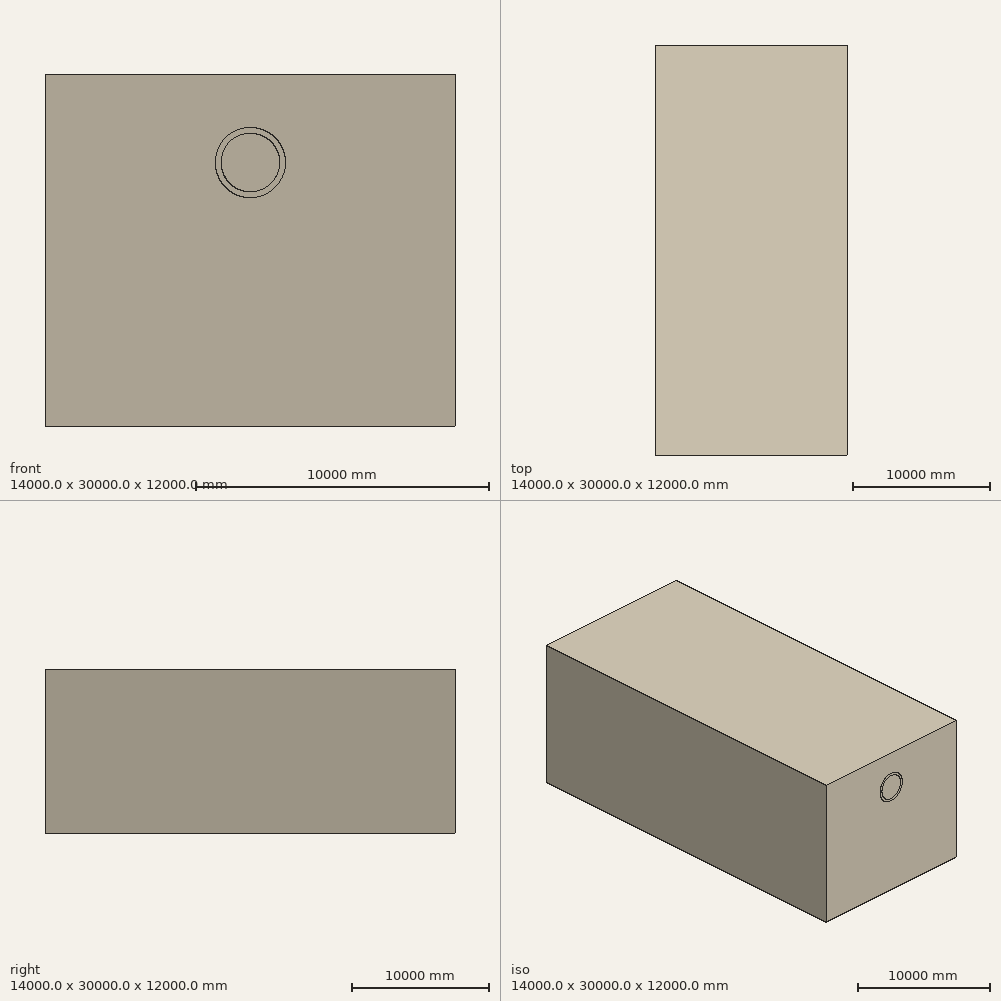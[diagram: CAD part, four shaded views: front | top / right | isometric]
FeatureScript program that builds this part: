
annotation { "Feature Type Name" : "Feature", "Feature Type Description" : "" }
export const myFeature = defineFeature(function(context is Context, id is Id, definition is map)
    precondition{}
    {
        {
            var Q0;
            Q0=qCreatedBy(makeId("Front.planeOp"),FACE);
            var sketch = newSketch(context, id + "F0", { "sketchPlane" : qUnion([Q0])});
            skCircle(sketch, "E0", {"center": v(0, 0) * mm, "radius": 1000 * mm});
            skLineSegment(sketch, "E1.bottom", {"start": v(-7000, 3000) * mm, "end": v(7000, 3000) * mm});
            skLineSegment(sketch, "E1.top", {"start": v(-7000, -9000) * mm, "end": v(7000, -9000) * mm});
            skLineSegment(sketch, "E1.left", {"start": v(-7000, 3000) * mm, "end": v(-7000, -9000) * mm});
            skLineSegment(sketch, "E1.right", {"start": v(7000, 3000) * mm, "end": v(7000, -9000) * mm});
            skCircle(sketch, "E2", {"center": v(0, 0) * mm, "radius": 1200 * mm});
            skSolve(sketch);
        }
        {
            var Q0;
            Q0=makeQuery(id+"F0.imprint","IMPRINT",FACE,{"disambiguationData":[TD([[makeQuery(id+"F0.imprint","IMPRINT",EDGE,{"derivedFrom":sQuery(id+"F0.wireOp",EDGE,"E1.bottom")}),-1.0]])]});
            extrude(context, id + "F1", {"entities" : qUnion([Q0]), "depth" : 30000 * mm, "offsetDistance" : 25 * mm});
        }
        {
            var Q0;
            Q0=makeQuery(id+"F1.opExtrude","CAP_FACE",FACE,{"disambiguationData":[OSD([sQuery(id+"F0.wireOp",EDGE,"E1.bottom"),sQuery(id+"F0.wireOp",EDGE,"E1.top"),sQuery(id+"F0.wireOp",EDGE,"E1.left"),sQuery(id+"F0.wireOp",EDGE,"E1.right"),sQuery(id+"F0.wireOp",EDGE,"E2")])],"isStart":true});
            var sketch = newSketch(context, id + "F2", { "sketchPlane" : qUnion([Q0])});
            skCircle(sketch, "E3", {"center": v(0, 0) * mm, "radius": 1200 * mm});
            skCircle(sketch, "E4", {"center": v(0, 0) * mm, "radius": 1000 * mm});
            skSolve(sketch);
        }
        {
            var Q0;
            Q0=makeQuery(id+"F2.imprint","IMPRINT",FACE,{"disambiguationData":[TD([[makeQuery(id+"F2.imprint","IMPRINT",EDGE,{"derivedFrom":sQuery(id+"F2.wireOp",EDGE,"E3")}),-1.0]])]});
            extrude(context, id + "F3", {"entities" : qUnion([Q0]), "depth" : -30000 * mm, "offsetDistance" : 25 * mm});
        }
        {
            var Q0;
            Q0=makeQuery(id+"F1.opExtrude","CAP_FACE",FACE,{"disambiguationData":[OSD([sQuery(id+"F0.wireOp",EDGE,"E1.bottom"),sQuery(id+"F0.wireOp",EDGE,"E1.top"),sQuery(id+"F0.wireOp",EDGE,"E1.left"),sQuery(id+"F0.wireOp",EDGE,"E1.right"),sQuery(id+"F0.wireOp",EDGE,"E2")])],"isStart":false});
            var sketch = newSketch(context, id + "F4", { "sketchPlane" : qUnion([Q0])});
            skCircle(sketch, "E5", {"center": v(0, 0) * mm, "radius": 1000 * mm});
            skSolve(sketch);
        }
        {
            var Q0;
            Q0=makeQuery(id+"F4.imprint","IMPRINT",FACE,{"disambiguationData":[TD([[makeQuery(id+"F4.imprint","IMPRINT",EDGE,{"derivedFrom":sQuery(id+"F4.wireOp",EDGE,"E5")}),1.0]])]});
            extrude(context, id + "F5", {"entities" : qUnion([Q0]), "depth" : -30000 * mm, "offsetDistance" : 25 * mm});
        }
    });
